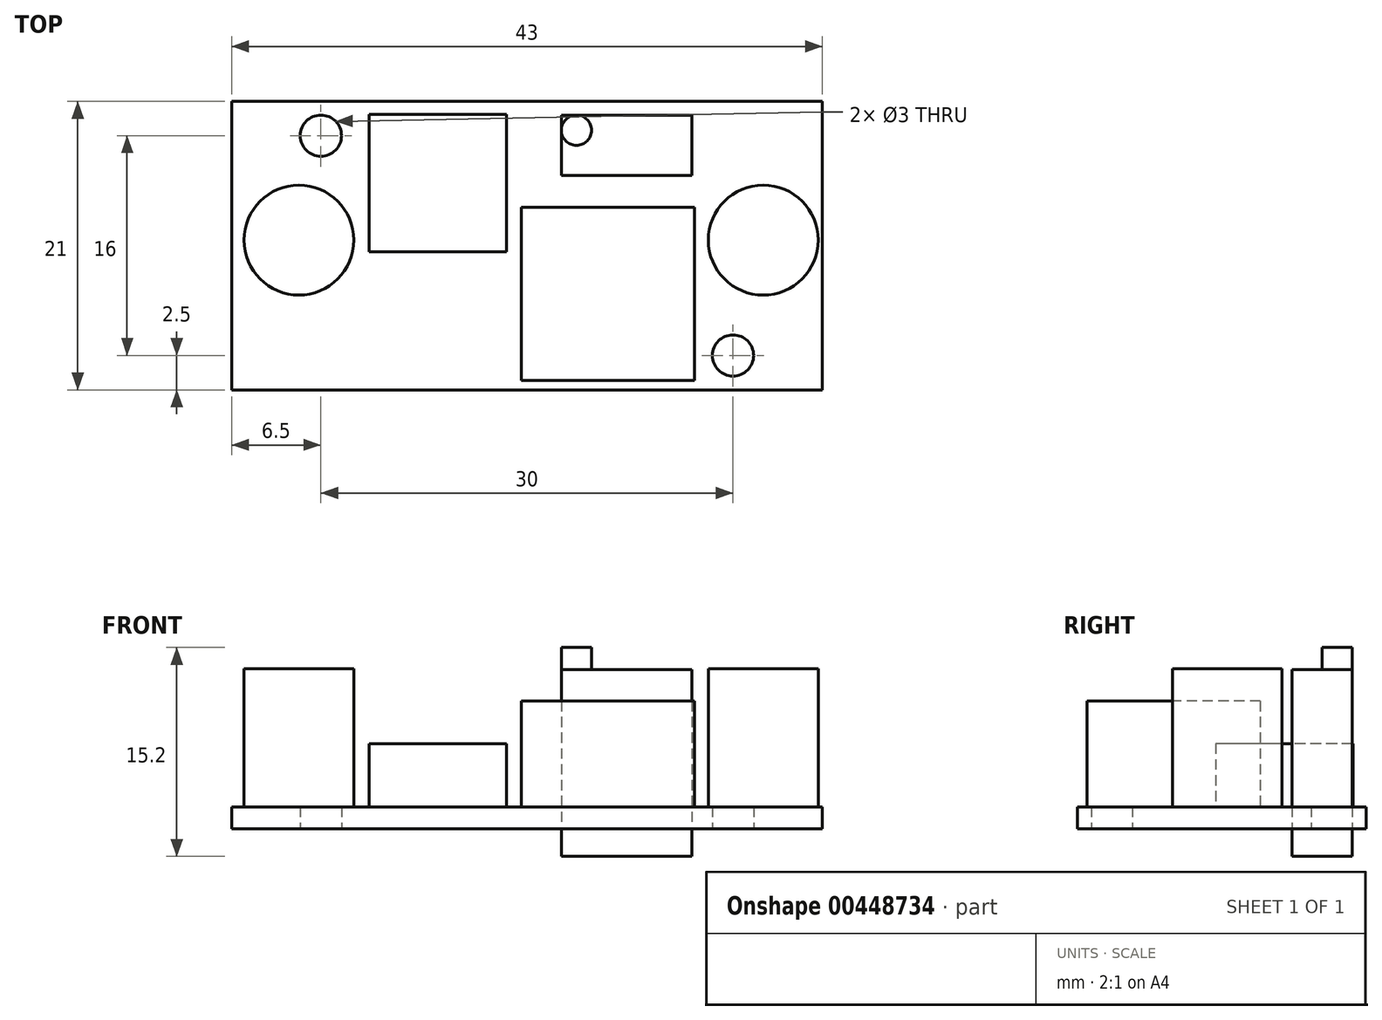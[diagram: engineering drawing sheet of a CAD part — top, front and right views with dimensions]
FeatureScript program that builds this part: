
annotation { "Feature Type Name" : "Feature", "Feature Type Description" : "" }
export const myFeature = defineFeature(function(context is Context, id is Id, definition is map)
    precondition{}
    {
        {
            var Q0;
            Q0=qCreatedBy(makeId("Top.planeOp"),FACE);
            var sketch = newSketch(context, id + "F0", { "sketchPlane" : qUnion([Q0])});
            skLineSegment(sketch, "E0.bottom", {"start": v(21.5, -10.5) * mm, "end": v(-21.5, -10.5) * mm});
            skLineSegment(sketch, "E0.top", {"start": v(21.5, 10.5) * mm, "end": v(-21.5, 10.5) * mm});
            skLineSegment(sketch, "E0.left", {"start": v(21.5, -10.5) * mm, "end": v(21.5, 10.5) * mm});
            skLineSegment(sketch, "E0.right", {"start": v(-21.5, -10.5) * mm, "end": v(-21.5, 10.5) * mm});
            skPoint(sketch, "E0.middle", {"position": v(0, 0) * mm});
            skCircle(sketch, "E1", {"center": v(-15, 8) * mm, "radius": 1.5 * mm});
            skCircle(sketch, "E2", {"center": v(15, -8) * mm, "radius": 1.5 * mm});
            skSolve(sketch);
        }
        {
            var Q0;
            Q0=makeQuery(id+"F0.imprint","IMPRINT",FACE,{"disambiguationData":[TD([[makeQuery(id+"F0.imprint","IMPRINT",EDGE,{"derivedFrom":sQuery(id+"F0.wireOp",EDGE,"E0.bottom")}),-1.0]])]});
            extrude(context, id + "F1", {"entities" : qUnion([Q0]), "depth" : 1.6 * mm});
        }
        {
            var Q0;
            Q0=makeQuery(id+"F1.opExtrude","CAP_FACE",FACE,{"disambiguationData":[OSD([sQuery(id+"F0.wireOp",EDGE,"E0.bottom"),sQuery(id+"F0.wireOp",EDGE,"E0.top"),sQuery(id+"F0.wireOp",EDGE,"E0.left"),sQuery(id+"F0.wireOp",EDGE,"E0.right"),sQuery(id+"F0.wireOp",EDGE,"E1"),sQuery(id+"F0.wireOp",EDGE,"E2")])],"isStart":false});
            cPlane(context, id + "F2", {"entities" : qUnion([Q0]), "cplaneType" : CPlaneType.OFFSET, "offset" : 0 * mm, "width" : 150 * mm, "height" : 150 * mm});
        }
        {
            var Q0;
            Q0=qCreatedBy(id+"F2.planeOp",FACE);
            var sketch = newSketch(context, id + "F3", { "sketchPlane" : qUnion([Q0])});
            skLineSegment(sketch, "E3.bottom", {"start": v(12, 5.1) * mm, "end": v(2.5, 5.1) * mm});
            skLineSegment(sketch, "E3.top", {"start": v(12, 9.5) * mm, "end": v(2.5, 9.5) * mm});
            skLineSegment(sketch, "E3.left", {"start": v(12, 5.1) * mm, "end": v(12, 9.5) * mm});
            skLineSegment(sketch, "E3.right", {"start": v(2.5, 5.1) * mm, "end": v(2.5, 9.5) * mm});
            skPoint(sketch, "E3.middle", {"position": v(7.25, 7.3) * mm});
            skLineSegment(sketch, "E4.bottom", {"start": v(-0.4, 2.8) * mm, "end": v(12.2, 2.8) * mm});
            skLineSegment(sketch, "E4.top", {"start": v(-0.4, -9.8) * mm, "end": v(12.2, -9.8) * mm});
            skLineSegment(sketch, "E4.left", {"start": v(-0.4, 2.8) * mm, "end": v(-0.4, -9.8) * mm});
            skLineSegment(sketch, "E4.right", {"start": v(12.2, 2.8) * mm, "end": v(12.2, -9.8) * mm});
            skCircle(sketch, "E5", {"center": v(-16.6, 0.4) * mm, "radius": 4 * mm});
            skCircle(sketch, "E6", {"center": v(17.2, 0.4) * mm, "radius": 4 * mm});
            skLineSegment(sketch, "E7.bottom", {"start": v(-11.5, 9.55) * mm, "end": v(-1.5, 9.55) * mm});
            skLineSegment(sketch, "E7.top", {"start": v(-11.5, -0.45) * mm, "end": v(-1.5, -0.45) * mm});
            skLineSegment(sketch, "E7.left", {"start": v(-11.5, 9.55) * mm, "end": v(-11.5, -0.45) * mm});
            skLineSegment(sketch, "E7.right", {"start": v(-1.5, 9.55) * mm, "end": v(-1.5, -0.45) * mm});
            skSolve(sketch);
        }
        {
            var Q0;
            Q0=makeQuery(id+"F3.imprint","IMPRINT",FACE,{"disambiguationData":[TD([[makeQuery(id+"F3.imprint","IMPRINT",EDGE,{"derivedFrom":sQuery(id+"F3.wireOp",EDGE,"E5")}),1.0]])]});
            extrude(context, id + "F4", {"entities" : qUnion([Q0]), "depth" : 10.05 * mm});
        }
        {
            var Q0;
            Q0=makeQuery(id+"F3.imprint","IMPRINT",FACE,{"disambiguationData":[TD([[makeQuery(id+"F3.imprint","IMPRINT",EDGE,{"derivedFrom":sQuery(id+"F3.wireOp",EDGE,"E6")}),1.0]])]});
            extrude(context, id + "F5", {"entities" : qUnion([Q0]), "depth" : 10.05 * mm});
        }
        {
            var Q0;
            Q0=makeQuery(id+"F3.imprint","IMPRINT",FACE,{"disambiguationData":[TD([[makeQuery(id+"F3.imprint","IMPRINT",EDGE,{"derivedFrom":sQuery(id+"F3.wireOp",EDGE,"E4.bottom")}),-1.0]])]});
            extrude(context, id + "F6", {"entities" : qUnion([Q0]), "depth" : 7.7 * mm});
        }
        {
            var Q0;
            Q0=makeQuery(id+"F3.imprint","IMPRINT",FACE,{"disambiguationData":[TD([[makeQuery(id+"F3.imprint","IMPRINT",EDGE,{"derivedFrom":sQuery(id+"F3.wireOp",EDGE,"E3.bottom")}),-1.0]])]});
            extrude(context, id + "F7", {"entities" : qUnion([Q0]), "depth" : 10 * mm, "hasSecondDirection" : true, "secondDirectionOppositeDirection" : true, "secondDirectionDepth" : 3.6 * mm});
        }
        {
            var Q0;
            Q0=makeQuery(id+"F3.imprint","IMPRINT",FACE,{"disambiguationData":[TD([[makeQuery(id+"F3.imprint","IMPRINT",EDGE,{"derivedFrom":sQuery(id+"F3.wireOp",EDGE,"E7.bottom")}),-1.0]])]});
            extrude(context, id + "F8", {"entities" : qUnion([Q0]), "depth" : 4.6 * mm});
        }
        {
            var Q0;
            Q0=makeQuery(id+"F7.opExtrude","CAP_FACE",FACE,{"disambiguationData":[OSD([sQuery(id+"F3.wireOp",EDGE,"E3.bottom"),sQuery(id+"F3.wireOp",EDGE,"E3.top"),sQuery(id+"F3.wireOp",EDGE,"E3.left"),sQuery(id+"F3.wireOp",EDGE,"E3.right")])],"isStart":false});
            cPlane(context, id + "F9", {"entities" : qUnion([Q0]), "cplaneType" : CPlaneType.OFFSET, "offset" : 0 * mm, "width" : 150 * mm, "height" : 150 * mm});
        }
        {
            var Q0;
            Q0=qCreatedBy(id+"F9.planeOp",FACE);
            var sketch = newSketch(context, id + "F10", { "sketchPlane" : qUnion([Q0])});
            skCircle(sketch, "E8", {"center": v(3.6, 8.4) * mm, "radius": 1.1 * mm});
            skSolve(sketch);
        }
        {
            var Q0;
            Q0=makeQuery(id+"F10.imprint","IMPRINT",FACE,{"disambiguationData":[TD([[makeQuery(id+"F10.imprint","IMPRINT",EDGE,{"derivedFrom":sQuery(id+"F10.wireOp",EDGE,"E8")}),1.0]])]});
            extrude(context, id + "F11", {"entities" : qUnion([Q0]), "depth" : 1.6 * mm});
        }
    });
